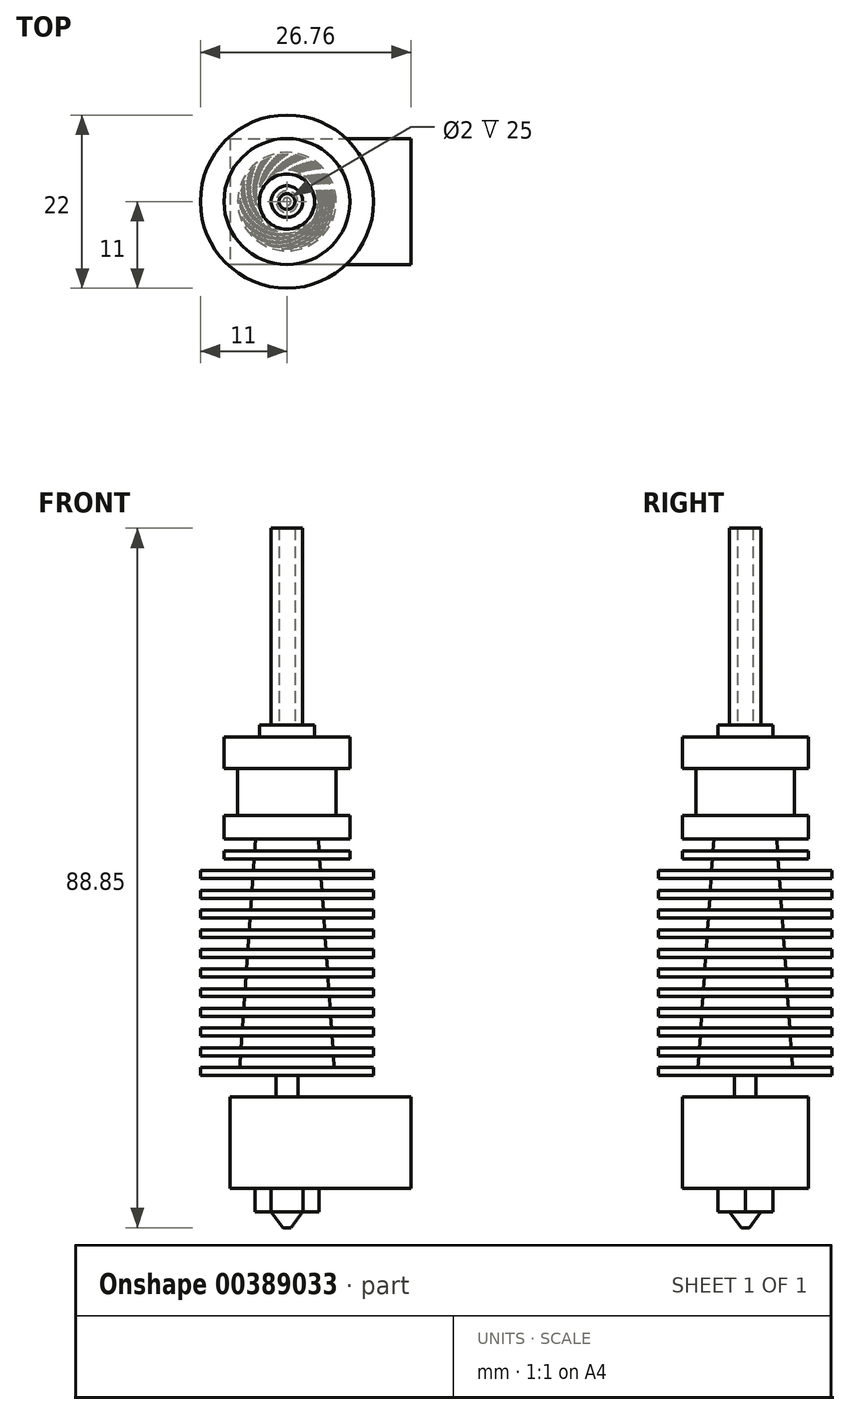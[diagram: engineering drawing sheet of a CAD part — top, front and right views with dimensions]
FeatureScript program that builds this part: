
annotation { "Feature Type Name" : "Feature", "Feature Type Description" : "" }
export const myFeature = defineFeature(function(context is Context, id is Id, definition is map)
    precondition{}
    {
        {
            var Q0;
            Q0=qCreatedBy(makeId("Right.planeOp"),FACE);
            var sketch = newSketch(context, id + "F0", { "sketchPlane" : qUnion([Q0])});
            skLineSegment(sketch, "E0", {"start": v(0, 0) * mm, "end": v(0.5, 0) * mm});
            skLineSegment(sketch, "E1", {"start": v(0, 2) * mm, "end": v(2, 2) * mm});
            skLineSegment(sketch, "E2", {"start": v(0, 2) * mm, "end": v(0, 0) * mm});
            skLineSegment(sketch, "E3", {"start": v(0.5, 0) * mm, "end": v(2, 2) * mm});
            skSolve(sketch);
        }
        {
            var Q0;
            Q0=qSketchRegion(id+"F0",true);
            var Q1;
            Q1=sQuery(id+"F0.wireOp",EDGE,"E2");
            revolve(context, id + "F1", {"entities" : qUnion([Q0]), "axis" : qUnion([Q1]), "revolveType" : RevolveType.FULL});
        }
        {
            var Q0;
            Q0=makeQuery(id+"F1.opRevolve","SWEPT_FACE",FACE,{"disambiguationData":[OSD([sQuery(id+"F0.wireOp",EDGE,"E1")])]});
            var sketch = newSketch(context, id + "F2", { "sketchPlane" : qUnion([Q0])});
            skLineSegment(sketch, "E4", {"start": v(-2.02, 3.5) * mm, "end": v(2.02, 3.5) * mm});
            skLineSegment(sketch, "E5", {"start": v(-2.02, -3.5) * mm, "end": v(2.02, -3.5) * mm});
            skLineSegment(sketch, "E6", {"start": v(-2.02, 3.5) * mm, "end": v(-4.04, 0) * mm});
            skLineSegment(sketch, "E7", {"start": v(-4.04, 0) * mm, "end": v(-2.02, -3.5) * mm});
            skLineSegment(sketch, "E8", {"start": v(2.02, -3.5) * mm, "end": v(4.04, 0) * mm});
            skLineSegment(sketch, "E9", {"start": v(4.04, 0) * mm, "end": v(2.02, 3.5) * mm});
            skLineSegment(sketch, "E10", {"start": v(4.04, 4.39) * mm, "end": v(4.04, -4.08) * mm, "construction": true});
            skLineSegment(sketch, "E11", {"start": v(-4.04, 3.84) * mm, "end": v(-4.04, -4.08) * mm, "construction": true});
            skSolve(sketch);
        }
        {
            var Q0;
            Q0=qSketchRegion(id+"F2",true);
            extrude(context, id + "F3", {"entities" : qUnion([Q0]), "operationType" : NewBodyOperationType.ADD, "depth" : 3 * mm});
        }
        {
            var Q0;
            Q0=makeQuery(id+"F3.opExtrude","CAP_FACE",FACE,{"disambiguationData":[OSD([sQuery(id+"F2.wireOp",EDGE,"E4"),sQuery(id+"F2.wireOp",EDGE,"E5"),sQuery(id+"F2.wireOp",EDGE,"E6"),sQuery(id+"F2.wireOp",EDGE,"E7"),sQuery(id+"F2.wireOp",EDGE,"E8"),sQuery(id+"F2.wireOp",EDGE,"E9")])],"isStart":false});
            var sketch = newSketch(context, id + "F4", { "sketchPlane" : qUnion([Q0])});
            skLineSegment(sketch, "E12", {"start": v(-4.04, 7.54) * mm, "end": v(-4.04, -6.8) * mm, "construction": true});
            skLineSegment(sketch, "E13", {"start": v(-7.24, 8) * mm, "end": v(-7.24, -8) * mm});
            skLineSegment(sketch, "E14", {"start": v(-7.24, 8) * mm, "end": v(15.76, 8) * mm});
            skLineSegment(sketch, "E15", {"start": v(15.76, 8) * mm, "end": v(15.76, -8) * mm});
            skLineSegment(sketch, "E16", {"start": v(15.76, -8) * mm, "end": v(-7.24, -8) * mm});
            skSolve(sketch);
        }
        {
            var Q0;
            Q0=qSketchRegion(id+"F4",true);
            extrude(context, id + "F5", {"entities" : qUnion([Q0]), "operationType" : NewBodyOperationType.ADD, "depth" : 11.6 * mm});
        }
        {
            var Q0;
            Q0=makeQuery(id+"F5.opExtrude","CAP_FACE",FACE,{"disambiguationData":[OSD([sQuery(id+"F4.wireOp",EDGE,"E13"),sQuery(id+"F4.wireOp",EDGE,"E14"),sQuery(id+"F4.wireOp",EDGE,"E15"),sQuery(id+"F4.wireOp",EDGE,"E16")])],"isStart":false});
            var sketch = newSketch(context, id + "F6", { "sketchPlane" : qUnion([Q0])});
            skCircle(sketch, "E17.0", {"center": v(0, 0) * mm, "radius": 2 * mm, "construction": true});
            skCircle(sketch, "E18", {"center": v(0, 0) * mm, "radius": 1.38 * mm});
            skSolve(sketch);
        }
        {
            var Q0;
            Q0=qSketchRegion(id+"F6",true);
            extrude(context, id + "F7", {"entities" : qUnion([Q0]), "operationType" : NewBodyOperationType.ADD, "depth" : 2.75 * mm});
        }
        {
            var Q0;
            Q0=qCreatedBy(makeId("Front.planeOp"),FACE);
            var sketch = newSketch(context, id + "F8", { "sketchPlane" : qUnion([Q0])});
            skLineSegment(sketch, "E19", {"start": v(0, 18.7) * mm, "end": v(0, 62.35) * mm});
            skLineSegment(sketch, "E20.0", {"start": v(-1.38, 19.35) * mm, "end": v(0, 19.35) * mm, "construction": true});
            skLineSegment(sketch, "E21", {"start": v(1.38, 19.35) * mm, "end": v(11, 19.35) * mm});
            skLineSegment(sketch, "E22", {"start": v(11, 19.35) * mm, "end": v(11, 20.35) * mm});
            skLineSegment(sketch, "E23", {"start": v(11, 20.35) * mm, "end": v(6, 20.35) * mm});
            skLineSegment(sketch, "E24", {"start": v(1.38, 19.35) * mm, "end": v(1.38, 20.35) * mm, "construction": true});
            skLineSegment(sketch, "E25", {"start": v(1.37, 20.35) * mm, "end": v(1.37, 21.85) * mm, "construction": true});
            skLineSegment(sketch, "E26", {"start": v(1.38, 19.35) * mm, "end": v(0, 19.35) * mm});
            skLineSegment(sketch, "E27.0.1.0", {"start": v(5.9, 21.85) * mm, "end": v(11, 21.85) * mm});
            skLineSegment(sketch, "E27.0.1.1", {"start": v(11, 21.85) * mm, "end": v(11, 22.85) * mm});
            skLineSegment(sketch, "E27.0.1.2", {"start": v(11, 22.85) * mm, "end": v(5.83, 22.85) * mm});
            skLineSegment(sketch, "E27.0.2.0", {"start": v(5.72, 24.35) * mm, "end": v(11, 24.35) * mm});
            skLineSegment(sketch, "E27.0.2.1", {"start": v(11, 24.35) * mm, "end": v(11, 25.35) * mm});
            skLineSegment(sketch, "E27.0.2.2", {"start": v(11, 25.35) * mm, "end": v(5.65, 25.35) * mm});
            skLineSegment(sketch, "E27.0.3.0", {"start": v(5.55, 26.85) * mm, "end": v(11, 26.85) * mm});
            skLineSegment(sketch, "E27.0.3.1", {"start": v(11, 26.85) * mm, "end": v(11, 27.85) * mm});
            skLineSegment(sketch, "E27.0.3.2", {"start": v(11, 27.85) * mm, "end": v(5.48, 27.85) * mm});
            skLineSegment(sketch, "E27.0.4.0", {"start": v(5.38, 29.35) * mm, "end": v(11, 29.35) * mm});
            skLineSegment(sketch, "E27.0.4.1", {"start": v(11, 29.35) * mm, "end": v(11, 30.35) * mm});
            skLineSegment(sketch, "E27.0.4.2", {"start": v(11, 30.35) * mm, "end": v(5.3, 30.35) * mm});
            skLineSegment(sketch, "E27.0.5.0", {"start": v(5.2, 31.85) * mm, "end": v(11, 31.85) * mm});
            skLineSegment(sketch, "E27.0.5.1", {"start": v(11, 31.85) * mm, "end": v(11, 32.85) * mm});
            skLineSegment(sketch, "E27.0.5.2", {"start": v(11, 32.85) * mm, "end": v(5.14, 32.85) * mm});
            skLineSegment(sketch, "E27.0.6.0", {"start": v(5.03, 34.35) * mm, "end": v(11, 34.35) * mm});
            skLineSegment(sketch, "E27.0.6.1", {"start": v(11, 34.35) * mm, "end": v(11, 35.35) * mm});
            skLineSegment(sketch, "E27.0.6.2", {"start": v(11, 35.35) * mm, "end": v(4.96, 35.35) * mm});
            skLineSegment(sketch, "E27.0.7.0", {"start": v(4.86, 36.85) * mm, "end": v(11, 36.85) * mm});
            skLineSegment(sketch, "E27.0.7.1", {"start": v(11, 36.85) * mm, "end": v(11, 37.85) * mm});
            skLineSegment(sketch, "E27.0.7.2", {"start": v(11, 37.85) * mm, "end": v(4.79, 37.85) * mm});
            skLineSegment(sketch, "E27.0.8.0", {"start": v(4.69, 39.35) * mm, "end": v(11, 39.35) * mm});
            skLineSegment(sketch, "E27.0.8.1", {"start": v(11, 39.35) * mm, "end": v(11, 40.35) * mm});
            skLineSegment(sketch, "E27.0.8.2", {"start": v(11, 40.35) * mm, "end": v(4.62, 40.35) * mm});
            skLineSegment(sketch, "E27.0.9.0", {"start": v(4.51, 41.85) * mm, "end": v(11, 41.85) * mm});
            skLineSegment(sketch, "E27.0.9.1", {"start": v(11, 41.85) * mm, "end": v(11, 42.85) * mm});
            skLineSegment(sketch, "E27.0.9.2", {"start": v(11, 42.85) * mm, "end": v(4.44, 42.85) * mm});
            skLineSegment(sketch, "E27.direction1", {"start": v(1.37, 19.35) * mm, "end": v(26.38, 19.35) * mm, "construction": true});
            skLineSegment(sketch, "E28", {"start": v(4.34, 44.35) * mm, "end": v(11, 44.35) * mm});
            skLineSegment(sketch, "E29", {"start": v(11, 44.35) * mm, "end": v(11, 45.35) * mm});
            skLineSegment(sketch, "E30", {"start": v(11, 45.35) * mm, "end": v(4.27, 45.35) * mm});
            skLineSegment(sketch, "E31", {"start": v(6, 20.35) * mm, "end": v(5.9, 21.85) * mm});
            skPoint(sketch, "E32.orphan", {"position": v(1.38, 21.85) * mm});
            skPoint(sketch, "E33.orphan", {"position": v(1.38, 24.35) * mm});
            skLineSegment(sketch, "E34.trimOffspring", {"start": v(5.83, 22.85) * mm, "end": v(5.72, 24.35) * mm});
            skLineSegment(sketch, "E35.trimOffspring", {"start": v(5.65, 25.35) * mm, "end": v(5.55, 26.85) * mm});
            skPoint(sketch, "E36.orphan", {"position": v(1.38, 26.85) * mm});
            skLineSegment(sketch, "E37.trimOffspring", {"start": v(5.48, 27.85) * mm, "end": v(5.38, 29.35) * mm});
            skPoint(sketch, "E38.orphan", {"position": v(1.38, 29.35) * mm});
            skPoint(sketch, "E39.orphan", {"position": v(1.38, 31.85) * mm});
            skPoint(sketch, "E40.orphan", {"position": v(1.38, 34.35) * mm});
            skPoint(sketch, "E41.orphan", {"position": v(1.38, 36.85) * mm});
            skPoint(sketch, "E42.orphan", {"position": v(1.38, 39.35) * mm});
            skPoint(sketch, "E43.orphan", {"position": v(1.38, 41.85) * mm});
            skLineSegment(sketch, "E44.trimOffspring", {"start": v(4.44, 42.85) * mm, "end": v(4.34, 44.35) * mm});
            skLineSegment(sketch, "E45.trimOffspring", {"start": v(4.62, 40.35) * mm, "end": v(4.51, 41.85) * mm});
            skLineSegment(sketch, "E46.trimOffspring", {"start": v(4.79, 37.85) * mm, "end": v(4.69, 39.35) * mm});
            skLineSegment(sketch, "E47.trimOffspring", {"start": v(4.96, 35.35) * mm, "end": v(4.86, 36.85) * mm});
            skLineSegment(sketch, "E48.trimOffspring", {"start": v(5.14, 32.85) * mm, "end": v(5.03, 34.35) * mm});
            skLineSegment(sketch, "E49.trimOffspring", {"start": v(5.3, 30.35) * mm, "end": v(5.2, 31.85) * mm});
            skLineSegment(sketch, "E50", {"start": v(4.27, 45.35) * mm, "end": v(4.17, 46.85) * mm});
            skLineSegment(sketch, "E51", {"start": v(0, 45.35) * mm, "end": v(0, 46.85) * mm});
            skLineSegment(sketch, "E52", {"start": v(4.17, 46.85) * mm, "end": v(8, 46.85) * mm});
            skLineSegment(sketch, "E53", {"start": v(8, 46.85) * mm, "end": v(8, 47.85) * mm});
            skLineSegment(sketch, "E54", {"start": v(8, 47.85) * mm, "end": v(4.1, 47.85) * mm});
            skLineSegment(sketch, "E55", {"start": v(4, 49.35) * mm, "end": v(8, 49.35) * mm});
            skLineSegment(sketch, "E56", {"start": v(8, 49.35) * mm, "end": v(8, 52.35) * mm});
            skLineSegment(sketch, "E57", {"start": v(8, 52.35) * mm, "end": v(6.25, 52.35) * mm});
            skLineSegment(sketch, "E58.trimOffspring", {"start": v(4.1, 47.85) * mm, "end": v(4, 49.35) * mm});
            skLineSegment(sketch, "E59", {"start": v(6.25, 52.35) * mm, "end": v(6.25, 58.35) * mm});
            skLineSegment(sketch, "E60", {"start": v(6.25, 58.35) * mm, "end": v(8, 58.35) * mm});
            skLineSegment(sketch, "E61", {"start": v(8, 58.35) * mm, "end": v(8, 62.35) * mm});
            skLineSegment(sketch, "E62", {"start": v(8, 62.35) * mm, "end": v(0, 62.35) * mm});
            skLineSegment(sketch, "E63", {"start": v(6, 20.35) * mm, "end": v(4, 49.35) * mm, "construction": true});
            skSolve(sketch);
        }
        {
            var Q0;
            Q0=qSketchRegion(id+"F8",true);
            var Q1;
            Q1=sQuery(id+"F8.wireOp",EDGE,"E19");
            revolve(context, id + "F9", {"operationType" : NewBodyOperationType.ADD, "entities" : qUnion([Q0]), "axis" : qUnion([Q1]), "revolveType" : RevolveType.FULL});
        }
        {
            var Q0;
            Q0=makeQuery(id+"F9.opRevolve","SWEPT_FACE",FACE,{"disambiguationData":[OSD([sQuery(id+"F8.wireOp",EDGE,"E62")])]});
            var sketch = newSketch(context, id + "F10", { "sketchPlane" : qUnion([Q0])});
            skCircle(sketch, "E64.0", {"center": v(0, 0) * mm, "radius": 8 * mm, "construction": true});
            skCircle(sketch, "E65", {"center": v(0, 0) * mm, "radius": 3.5 * mm});
            skSolve(sketch);
        }
        {
            var Q0;
            Q0=qSketchRegion(id+"F10",true);
            extrude(context, id + "F11", {"entities" : qUnion([Q0]), "operationType" : NewBodyOperationType.ADD, "depth" : 1.5 * mm});
        }
        {
            var Q0;
            Q0=makeQuery(id+"F11.opExtrude","CAP_FACE",FACE,{"disambiguationData":[OSD([sQuery(id+"F10.wireOp",EDGE,"E65")])],"isStart":false});
            var sketch = newSketch(context, id + "F12", { "sketchPlane" : qUnion([Q0])});
            skCircle(sketch, "E66.0", {"center": v(0, 0) * mm, "radius": 3.5 * mm, "construction": true});
            skCircle(sketch, "E67", {"center": v(0, 0) * mm, "radius": 2 * mm});
            skCircle(sketch, "E68", {"center": v(0, 0) * mm, "radius": 1 * mm});
            skSolve(sketch);
        }
        {
            var Q0;
            Q0=qSketchRegion(id+"F12",true);
            extrude(context, id + "F13", {"entities" : qUnion([Q0]), "operationType" : NewBodyOperationType.ADD, "depth" : 25 * mm});
        }
    });
